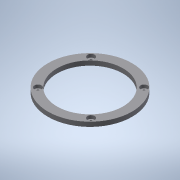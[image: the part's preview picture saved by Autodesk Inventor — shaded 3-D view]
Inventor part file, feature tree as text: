
AUTODESK INVENTOR PART (.ipt)
format: ipt  version: 2021 (Build 250183000, 183)  size: 117,248 bytes
history: native  units: in
note: dims shown in document units (in); Inventor stores cm internally (conversion verified against a paired STEP export)
features: sketch x2, extrude x1, hole x1
ambient origin geometry x8: Origin, YZ Plane, XZ Plane, XY Plane, X Axis, Y Axis, Z Axis, Center Point
bodies: Solid1 (feature_tree)
feature tree (4):
  extrude  "Extrusion1"  Depth=2.2047in
  hole  "Hole3"  [1 undecoded]
  sketch  "Sketch1"  dims[d0=1.7323in d1=2.2047in]
  sketch  "Sketch5"  dims[d2=0.1181in d3=0.0in d22=1.3919in d23=1.3919in d24=0.096in d25=0.2362in d26=0.1875in d27=0.086in d28=90.0deg d29=0.315in d30=0.8108in]
note: 1 required parameter value undecoded (feature->parameter linkage not recoverable at this tier; creation-order binding heuristic only, values carry confidence <= 0.55)
